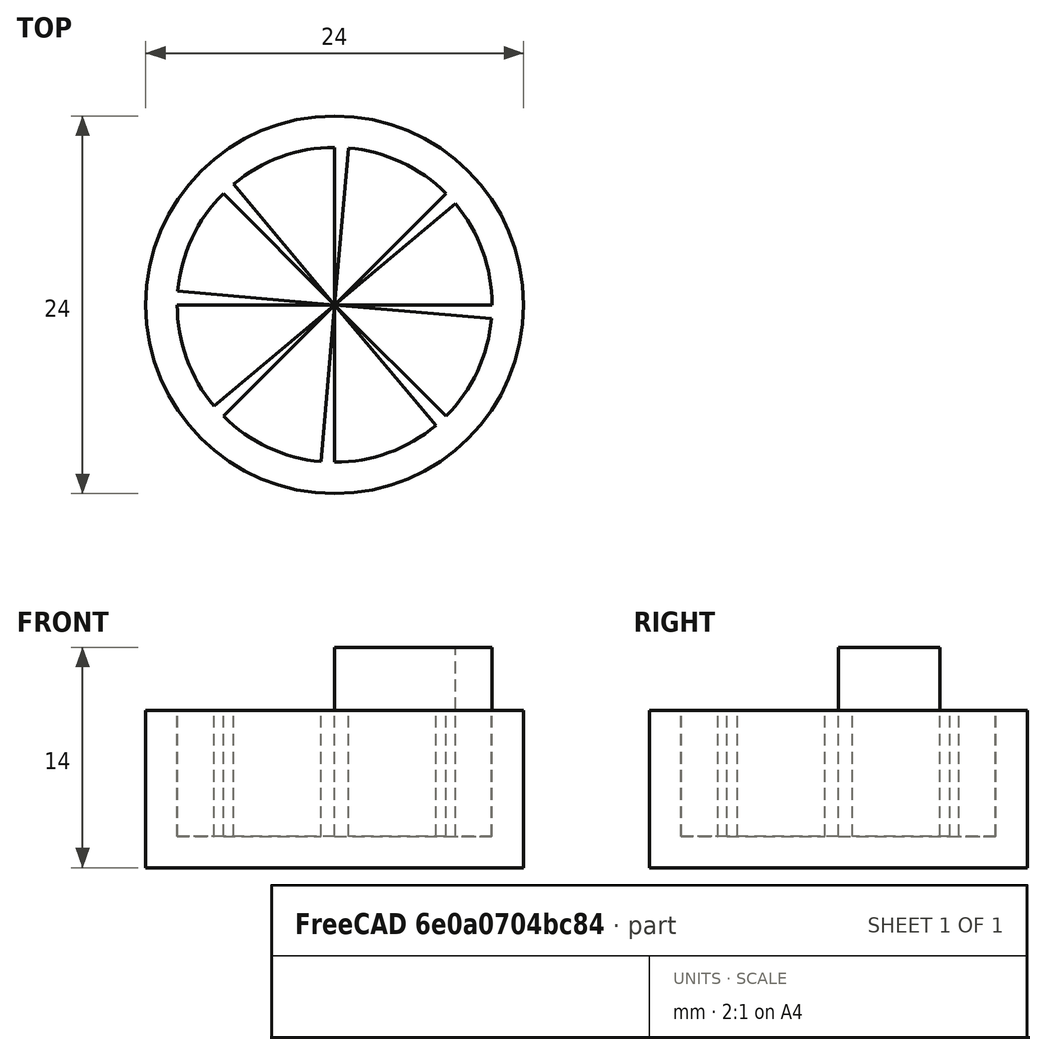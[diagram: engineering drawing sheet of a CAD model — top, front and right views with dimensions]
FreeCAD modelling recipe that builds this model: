
FCSTD DOCUMENT  (FreeCAD 0.21R33694 (Git))
Label: OJT1_T011R010_tribial
License: All rights reserved
LicenseURL: http://en.wikipedia.org/wiki/All_rights_reserved
objects: Part::Cylinder×2, Part::FeaturePython×1, Part::Cut×1
note: 3 computed .brp shape members not serialized (recipe doc carries the construction recipe); baked Part::Feature solids carry a one-line shape summary decoded from their .brp

FEATURE [Part::Cylinder] Cylinder  label="caixa"
  Angle = 360
  AttacherType = Attacher::AttachEngine3D
  FirstAngle = 0
  Height = 10
  Radius = 12
  SecondAngle = 0
FEATURE [Part::Cylinder] Cylinder001  label="quesito"
  Angle = 40
  AttacherType = Attacher::AttachEngine3D
  FirstAngle = 0
  Height = 12
  Placement = pos=(0,0,2) rot=(0,0,1;0rad)
  Radius = 10
  SecondAngle = 0
FEATURE [Part::FeaturePython] Array  # Draft array (typed FeaturePython)
  AlwaysSyncPlacement = false
  Angle = 360
  ArrayType = 1
  Axis = (0,0,1)
  Base = -> Cylinder001
  Center = (0,0,0)
  Count = 8
  ExpandArray = false
  Fuse = false
  IntervalAxis = (0,0,0)
  IntervalX = (50,0,0)
  IntervalY = (0,50,0)
  IntervalZ = (0,0,50)
  NumberCircles = 3
  NumberPolar = 8
  NumberX = 2
  NumberY = 2
  NumberZ = 1
  PlacementList = 8 placements: [(0,0,2),(0,0,2),(0,0,2),(0,0,2),(0,0,2),(0,0,2),(0,0,2),(0,0,2)]
  RadialDistance = 50
  ScaleList = (8) [(1,1,1),(1,1,1),(1,1,1),(1,1,1),(1,1,1),(1,1,1),(1,1,1),(1,1,1)]
  Symmetry = 1
  TangentialDistance = 25
FEATURE [Part::Cut] Cut
  Base = -> Cylinder
  Refine = true
  Tool = -> Array
